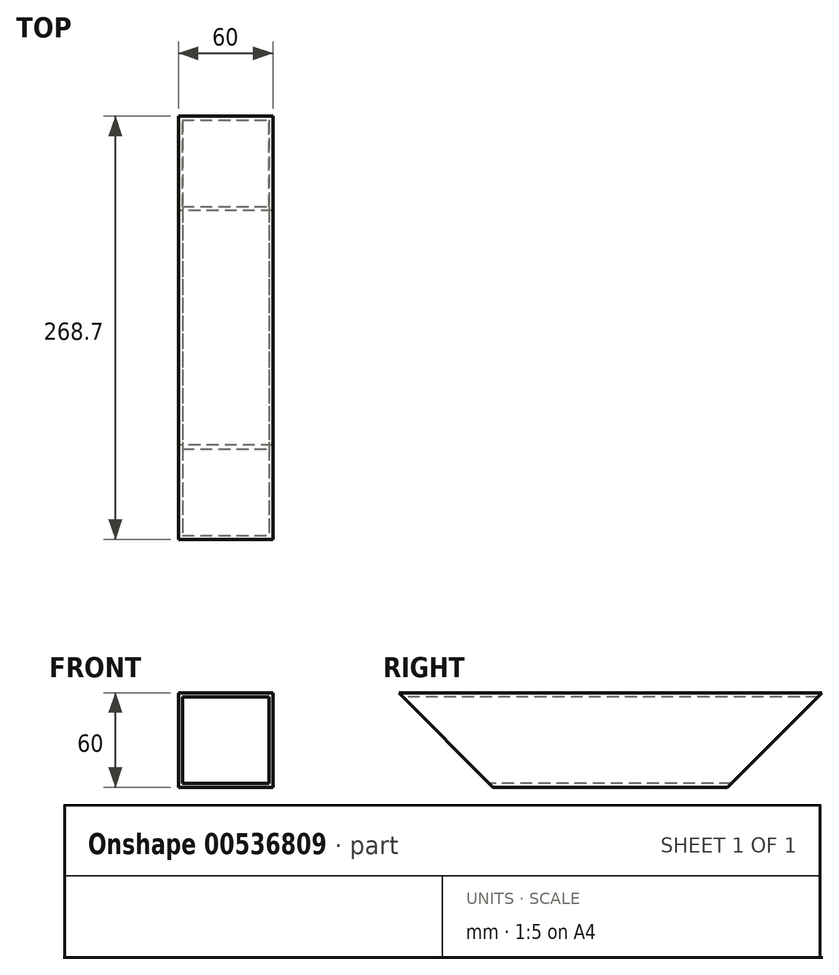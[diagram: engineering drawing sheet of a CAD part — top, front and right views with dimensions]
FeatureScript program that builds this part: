
annotation { "Feature Type Name" : "Feature", "Feature Type Description" : "" }
export const myFeature = defineFeature(function(context is Context, id is Id, definition is map)
    precondition{}
    {
        {
            var Q0;
            Q0=qCreatedBy(makeId("Front.planeOp"),FACE);
            var sketch = newSketch(context, id + "F0", { "sketchPlane" : qUnion([Q0])});
            skLineSegment(sketch, "E0.bottom", {"start": v(-30, -30) * mm, "end": v(30, -30) * mm});
            skLineSegment(sketch, "E0.top", {"start": v(-30, 30) * mm, "end": v(30, 30) * mm});
            skLineSegment(sketch, "E0.left", {"start": v(-30, -30) * mm, "end": v(-30, 30) * mm});
            skLineSegment(sketch, "E0.right", {"start": v(30, -30) * mm, "end": v(30, 30) * mm});
            skPoint(sketch, "E0.middle", {"position": v(0, 0) * mm});
            skLineSegment(sketch, "E1.bottom", {"start": v(-27.5, -27.5) * mm, "end": v(27.5, -27.5) * mm});
            skLineSegment(sketch, "E1.top", {"start": v(-27.5, 27.5) * mm, "end": v(27.5, 27.5) * mm});
            skLineSegment(sketch, "E1.left", {"start": v(-27.5, -27.5) * mm, "end": v(-27.5, 27.5) * mm});
            skLineSegment(sketch, "E1.right", {"start": v(27.5, -27.5) * mm, "end": v(27.5, 27.5) * mm});
            skSolve(sketch);
        }
        {
            var Q0;
            Q0=makeQuery(id+"F0.imprint","IMPRINT",FACE,{"disambiguationData":[TD([[makeQuery(id+"F0.imprint","IMPRINT",EDGE,{"derivedFrom":sQuery(id+"F0.wireOp",EDGE,"E0.bottom")}),1.0]])]});
            extrude(context, id + "F1", {"entities" : qUnion([Q0]), "oppositeDirection" : true, "depth" : 268.7 * mm, "offsetDistance" : 25 * mm});
        }
        {
            var Q0;
            Q0=makeQuery(id+"F1.opExtrude","SWEPT_FACE",FACE,{"disambiguationData":[OSD([sQuery(id+"F0.wireOp",EDGE,"E0.left")])]});
            var sketch = newSketch(context, id + "F2", { "sketchPlane" : qUnion([Q0])});
            skLineSegment(sketch, "E2", {"start": v(-268.7, 30) * mm, "end": v(-208.7, -30) * mm});
            skLineSegment(sketch, "E3", {"start": v(0, 30) * mm, "end": v(-60, -30) * mm});
            skSolve(sketch);
        }
        {
            var Q0;
            {var subQ0=sQuery(id+"F2.wireOp",EDGE,"E3");Q0=makeQuery(id+"F2.imprint","IMPRINT",FACE,{"disambiguationData":[TD([[makeQuery(id+"F2.imprint","IMPRINT",EDGE,{"derivedFrom":subQ0}),1.0]])]});}
            var Q1;
            {var subQ0=sQuery(id+"F2.wireOp",EDGE,"E2");Q1=makeQuery(id+"F2.imprint","IMPRINT",FACE,{"disambiguationData":[TD([[makeQuery(id+"F2.imprint","IMPRINT",EDGE,{"derivedFrom":subQ0}),-1.0]])]});}
            extrude(context, id + "F3", {"entities" : qUnion([Q0, Q1]), "operationType" : NewBodyOperationType.REMOVE, "oppositeDirection" : true, "depth" : 75 * mm, "offsetDistance" : 25 * mm, "hasSecondDirection" : true, "secondDirectionOppositeDirection" : false, "secondDirectionDepth" : 75 * mm});
        }
    });
